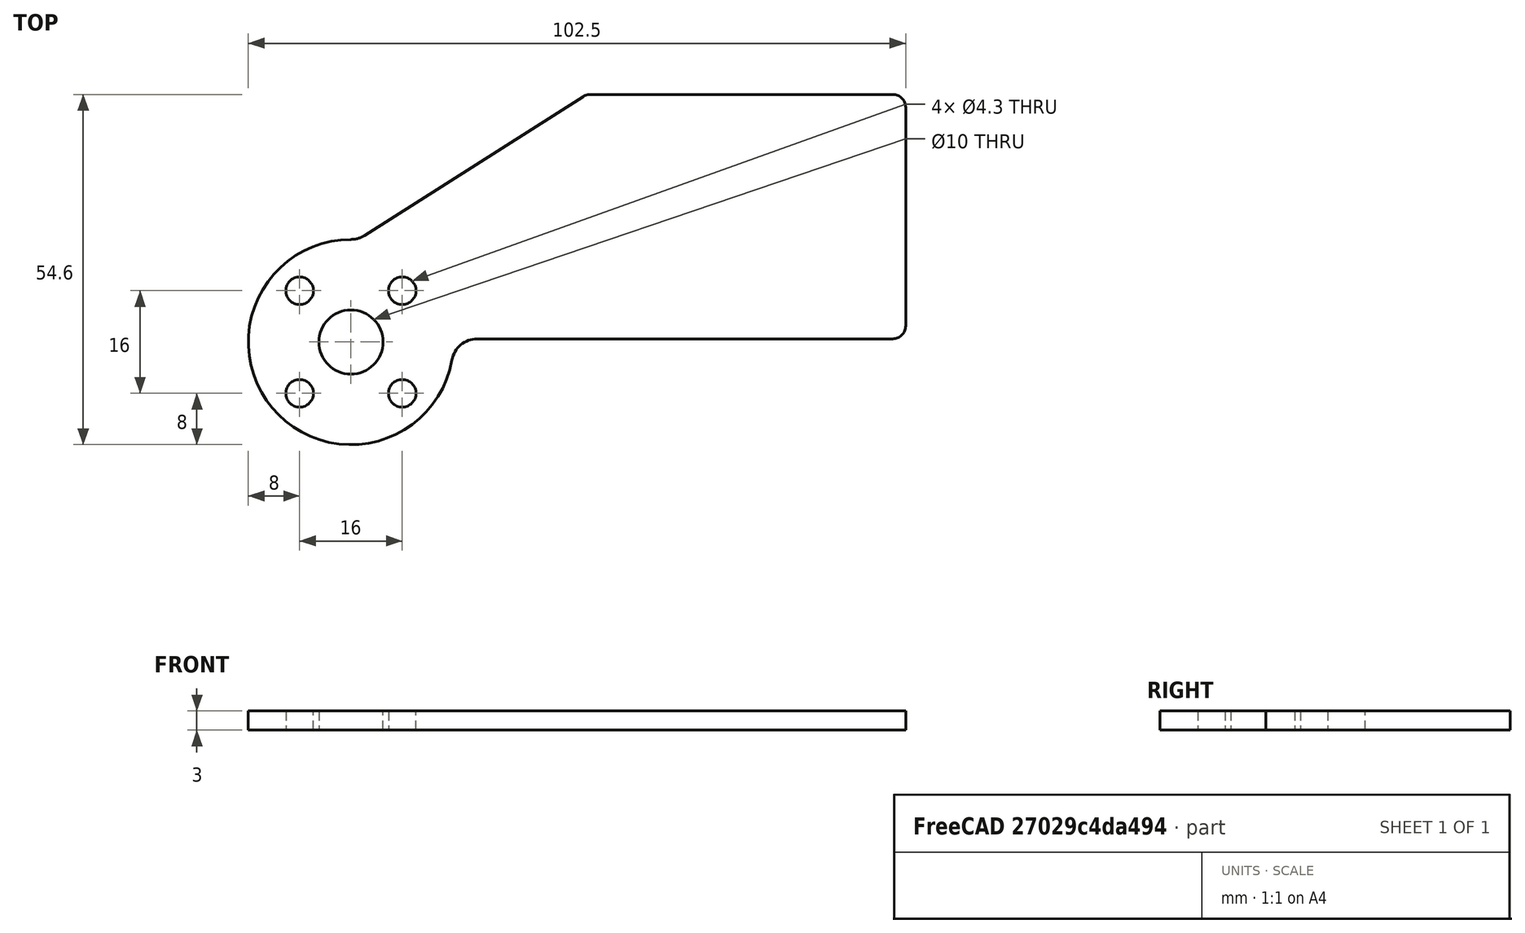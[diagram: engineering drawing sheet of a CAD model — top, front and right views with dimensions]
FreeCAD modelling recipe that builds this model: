
FCSTD DOCUMENT  (FreeCAD 0.20R29603 (Git))
Label: tmaze_door_1p5in
License: All rights reserved
LicenseURL: http://en.wikipedia.org/wiki/All_rights_reserved
objects: Sketcher::SketchObject×2, Spreadsheet::Sheet×1, PartDesign::Pad×1, PartDesign::Body×1, Part::Part2DObjectPython×1
note: 6 computed .brp shape members not serialized (recipe doc carries the construction recipe); baked Part::Feature solids carry a one-line shape summary decoded from their .brp

FEATURE [Sketcher::SketchObject] Sketch  label="DoorSketch"
  FullyConstrained = true
  MapMode = 5
  Support = -> [XY_Plane]
  expr: Constraints[11] = Spreadsheet.DoorFilletRadius
  expr: Constraints[1] = Spreadsheet.DoorHubDiameter
  expr: Constraints[29] = Spreadsheet.DoorToMazeFloorMargin
  expr: Constraints[34] = Spreadsheet.DoorHubFilletRadius
  expr: Constraints[3] = Spreadsheet.DoorLength
  expr: Constraints[40] = Spreadsheet.ServoSplineToMazeFloorDistance
  expr: Constraints[58] = Spreadsheet.ServoHubMountThruHoleDiameter
  expr: Constraints[59] = Spreadsheet.ServoHubMountHoleSpacing
  expr: Constraints[5] = Spreadsheet.DoorHeight
  expr: Constraints[61] = Spreadsheet.ServoHubCenterHoleDiameter
  sketch-geometry (26):
    g0: Circle CenterX=0 CenterY=0 CenterZ=0 NormalX=0 NormalY=0 NormalZ=1 AngleXU=0 Radius=16
    g1: LineSegment StartX=36.7 StartY=0.5 StartZ=0 EndX=84.5 EndY=0.5 EndZ=0
    g2: LineSegment StartX=86.5 StartY=2.5 StartZ=0 EndX=86.5 EndY=36.6 EndZ=0
    g3: LineSegment StartX=84.5 StartY=38.6 StartZ=0 EndX=37.2821 EndY=38.6 EndZ=0
    g4: LineSegment StartX=2.14658 StartY=16.6248 StartZ=0 EndX=36.2088 EndY=38.2876 EndZ=0
    g5: ArcOfCircle CenterX=84.5 CenterY=2.5 CenterZ=0 NormalX=0 NormalY=0 NormalZ=1 AngleXU=0 Radius=2 StartAngle=4.71239 EndAngle=6.28319
    g6: GeomPoint X=86.5 Y=0.5 Z=0
    g7: ArcOfCircle CenterX=84.5 CenterY=36.6 CenterZ=0 NormalX=0 NormalY=0 NormalZ=1 AngleXU=0 Radius=2 StartAngle=6e-16 EndAngle=1.5708
    g8: GeomPoint X=86.5 Y=38.6 Z=0
    g9: LineSegment StartX=36.7 StartY=38.6 StartZ=0 EndX=36.7 EndY=0.5 EndZ=0
    g10: ArcOfCircle CenterX=37.2821 CenterY=36.6 CenterZ=0 NormalX=0 NormalY=0 NormalZ=1 AngleXU=0 Radius=2 StartAngle=1.5708 EndAngle=2.13725
    g11: GeomPoint X=36.7 Y=38.6 Z=0
    g12: ArcOfCircle CenterX=0 CenterY=0 CenterZ=0 NormalX=0 NormalY=0 NormalZ=1 AngleXU=0 Radius=16 StartAngle=1.5708 EndAngle=6.10728
    g13: LineSegment StartX=36.7 StartY=0 StartZ=0 EndX=36.7 EndY=0.5 EndZ=0
    g14: LineSegment StartX=36.7 StartY=0.5 StartZ=0 EndX=19.6914 EndY=0.5 EndZ=0
    g15: ArcOfCircle CenterX=19.6914 CenterY=-3.5 CenterZ=0 NormalX=0 NormalY=0 NormalZ=1 AngleXU=0 Radius=4 StartAngle=1.5708 EndAngle=2.96569
    g16: ArcOfCircle CenterX=5e-16 CenterY=20 CenterZ=0 NormalX=0 NormalY=0 NormalZ=1 AngleXU=0 Radius=4 StartAngle=4.71239 EndAngle=5.27884
    g17: LineSegment StartX=-8 StartY=8 StartZ=0 EndX=8 EndY=8 EndZ=0
    g18: LineSegment StartX=8 StartY=8 StartZ=0 EndX=8 EndY=-8 EndZ=0
    g19: LineSegment StartX=8 StartY=-8 StartZ=0 EndX=-8 EndY=-8 EndZ=0
    g20: LineSegment StartX=-8 StartY=-8 StartZ=0 EndX=-8 EndY=8 EndZ=0
    g21: Circle CenterX=-8 CenterY=8 CenterZ=0 NormalX=0 NormalY=0 NormalZ=1 AngleXU=0 Radius=2.15
    g22: Circle CenterX=8 CenterY=8 CenterZ=0 NormalX=0 NormalY=0 NormalZ=1 AngleXU=0 Radius=2.15
    g23: Circle CenterX=-8 CenterY=-8 CenterZ=0 NormalX=0 NormalY=0 NormalZ=1 AngleXU=0 Radius=2.15
    g24: Circle CenterX=8 CenterY=-8 CenterZ=0 NormalX=0 NormalY=0 NormalZ=1 AngleXU=0 Radius=2.15
    g25: Circle CenterX=0 CenterY=0 CenterZ=0 NormalX=0 NormalY=0 NormalZ=1 AngleXU=0 Radius=5
  constraints (62):
    c: Coincident(g0,g-1)
    c: Diameter(g0) = 32
    c: Horizontal(g1)
    c: DistanceX(g1,g6) = 49.8
    c: Vertical(g2)
    c: DistanceY(g6,g8) = 38.1
    c: Horizontal(g3)
    c: PointOnObject(g6,g1)
    c: PointOnObject(g6,g2)
    c: Tangent(g1,g5) = -1.5708
    c: Tangent(g2,g5) = -1.5708
    c: Radius(g5) = 2
    c: PointOnObject(g8,g3)
    c: PointOnObject(g8,g2)
    c: Tangent(g3,g7) = -1.5708
    c: Tangent(g2,g7) = -1.5708
    c: Equal(g5,g7)
    c: Coincident(g9,g11)
    c: Vertical(g9)
    c: PointOnObject(g11,g4)
    c: PointOnObject(g11,g3)
    c: Tangent(g4,g10) = 1.5708
    c: Tangent(g3,g10) = -1.5708
    c: Equal(g7,g10)
    c: Coincident(g12,g0)
    c: PointOnObject(g12,g0)
    c: PointOnObject(g13,g-1)
    c: Vertical(g13)
    c: Coincident(g13,g1)
    c: DistanceY(g13,g13) = 0.5
    c: Coincident(g14,g1)
    c: Horizontal(g14)
    c: Tangent(g15,g14) = -1.5708
    c: Tangent(g15,g12) = 1.5708
    c: Radius(g15) = 4
    c: Tangent(g12,g16) = 1.5708
    c: Tangent(g4,g16) = -1.5708
    c: Equal(g16,g15)
    c: PointOnObject(g12,g-2)
    c: Coincident(g9,g1)
    c: DistanceX(g12,g1) = 36.7
    c: Coincident(g17,g18)
    c: Coincident(g18,g19)
    c: Coincident(g19,g20)
    c: Coincident(g20,g17)
    c: Horizontal(g17)
    c: Horizontal(g19)
    c: Vertical(g18)
    c: Vertical(g20)
    c: Symmetric(g17,g18,g12)
    c: Equal(g20,g17)
    c: Coincident(g21,g17)
    c: Coincident(g22,g17)
    c: Coincident(g23,g19)
    c: Coincident(g24,g18)
    c: Equal(g21,g22)
    c: Equal(g22,g24)
    c: Equal(g24,g23)
    c: Diameter(g21) = 4.3
    c: DistanceX(g17,g17) = 16
    c: Coincident(g25,g12)
    c: Diameter(g25) = 10
FEATURE [Spreadsheet::Sheet] Spreadsheet
  cells = A2=Servo Hub Parameters; A3=ServoHubDiameter; B3(ServoHubDiameter)==32mm; A4=ServoHubMountHoleSpacing; B4(ServoHubMountHoleSpacing)==16mm; A5=ServoHubMountThruHoleDiameter; B5(ServoHubMountThruHoleDiameter)==4.3mm; A6=ServoHubCenterHoleDiameter; B6(ServoHubCenterHoleDiameter)==10mm; A7=ServoSplineToServoMountHoleDistance; B7(ServoSplineToServoMountHoleDistance)==14.2mm; A8=ServoMountHoleToBracketBndryDistance; B8(ServoMountHoleToBracketBndryDistance)==3.5mm; A9=ServoMarginToMountPlate; B9(ServoMarginToMountPlate)==10mm; A10=MountPlateThickness; B10(MountPlateThickness)==9mm; A11=MazeWidth; B11(MazeWidth)==2in; A14=Design Parameters; A15=DoorHubDiameter; B15(DoorHubDiameter)==ServoHubDiameter; A16=DoorToMazeFloorMargin; B16(DoorToMazeFloorMargin)==0.5mm; A17=DoorToMazeWallMargin; B17(DoorToMazeWallMargin)==1mm; A18=ServoSplineToMazeFloorDistance; B18(ServoSplineToMazeFloorDistance)==ServoSplineToServoMountHoleDistance + ServoMountHoleToBracketBndryDistance + ServoMarginToMountPlate + MountPlateThickness; A19=DoorLength; B19(DoorLength)==MazeWidth - DoorToMazeWallMargin; A20=DoorHeight; B20(DoorHeight)==1.5in; A21=DoorFilletRadius; B21(DoorFilletRadius)==2mm; A22=DoorHubFilletRadius; B22(DoorHubFilletRadius)==4mm; A23=DoorThickness; B23(DoorThickness)==3mm
FEATURE [PartDesign::Pad] Pad
  Direction = (0,0,1)
  Length = 3
  Length2 = 10
  Profile = -> Sketch
  ReferenceAxis = -> Sketch [N_Axis]
  Type = 0
  expr: Length = Spreadsheet.DoorThickness
FEATURE [PartDesign::Body] Body
  Group = -> [Sketch,Pad]
  Origin = -> Origin
  Tip = -> Pad
FEATURE [Part::Part2DObjectPython] Shape2DView  # Draft 2D object (typed FeaturePython)
  AutoUpdate = true
  Base = -> Pad
  Clip = false
  FaceNumbers = [17]
  FuseArch = false
  HiddenLines = false
  InPlace = true
  OnlySolids = false
  Projection = (0,0,1)
  ProjectionMode = 0
  SegmentLength = 0.05
  Tessellation = false
  VisibleOnly = false
FEATURE [Sketcher::SketchObject] Sketch001
  FullyConstrained = false
  sketch-geometry (16):
    g0: LineSegment StartX=36.7 StartY=0.5 StartZ=0 EndX=84.5 EndY=0.5 EndZ=0
    g1: ArcOfCircle CenterX=84.5 CenterY=2.5 CenterZ=0 NormalX=0 NormalY=0 NormalZ=1 AngleXU=0 Radius=2 StartAngle=4.71239 EndAngle=6.28319
    g2: LineSegment StartX=86.5 StartY=2.5 StartZ=0 EndX=86.5 EndY=36.6 EndZ=0
    g3: ArcOfCircle CenterX=84.5 CenterY=36.6 CenterZ=0 NormalX=0 NormalY=0 NormalZ=1 AngleXU=0 Radius=2 StartAngle=1e-15 EndAngle=1.5708
    g4: LineSegment StartX=84.5 StartY=38.6 StartZ=0 EndX=37.2821 EndY=38.6 EndZ=0
    g5: ArcOfCircle CenterX=37.2821 CenterY=36.6 CenterZ=0 NormalX=0 NormalY=0 NormalZ=1 AngleXU=0 Radius=2 StartAngle=1.5708 EndAngle=2.13725
    g6: LineSegment StartX=2.14658 StartY=16.6248 StartZ=0 EndX=36.2088 EndY=38.2876 EndZ=0
    g7: ArcOfCircle CenterX=5e-16 CenterY=20 CenterZ=0 NormalX=0 NormalY=0 NormalZ=1 AngleXU=0 Radius=4 StartAngle=4.71239 EndAngle=5.27884
    g8: ArcOfCircle CenterX=0 CenterY=0 CenterZ=0 NormalX=0 NormalY=0 NormalZ=1 AngleXU=0 Radius=16 StartAngle=1.5708 EndAngle=6.10728
    g9: ArcOfCircle CenterX=19.6914 CenterY=-3.5 CenterZ=0 NormalX=0 NormalY=0 NormalZ=1 AngleXU=0 Radius=4 StartAngle=1.5708 EndAngle=2.96569
    g10: LineSegment StartX=36.7 StartY=0.5 StartZ=0 EndX=19.6914 EndY=0.5 EndZ=0
    g11: Circle CenterX=0 CenterY=0 CenterZ=0 NormalX=0 NormalY=0 NormalZ=1 AngleXU=0 Radius=5
    g12: Circle CenterX=8 CenterY=-8 CenterZ=0 NormalX=0 NormalY=0 NormalZ=1 AngleXU=0 Radius=2.15
    g13: Circle CenterX=-8 CenterY=-8 CenterZ=0 NormalX=0 NormalY=0 NormalZ=1 AngleXU=0 Radius=2.15
    g14: Circle CenterX=8 CenterY=8 CenterZ=0 NormalX=0 NormalY=0 NormalZ=1 AngleXU=0 Radius=2.15
    g15: Circle CenterX=-8 CenterY=8 CenterZ=0 NormalX=0 NormalY=0 NormalZ=1 AngleXU=0 Radius=2.15
